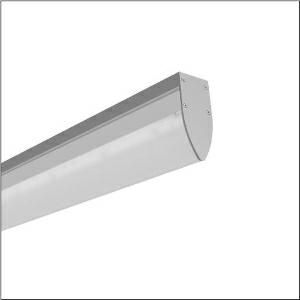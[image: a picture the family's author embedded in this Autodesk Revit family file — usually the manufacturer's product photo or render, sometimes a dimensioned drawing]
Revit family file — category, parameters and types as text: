
# Revit family: mira_21_td_51fr527d434a
name_source: partatom
category: Lighting Fixtures
units: mm (PartAtom-declared; Revit-internal decimal feet)

## family parameters
Cut with Voids When Loaded = No
Host = Face
Light Source = No
Part Type = Normal
Room Calculation Point = No
Round Connector Dimension = Use Diameter
Shared = No

## types (1)
- Mira 21 TD (1 x LED, 3660 lm, 26 W, 4000K)
    Apparent Load = 26 VA
    CIE Flux Codes = 40 68 87 81 100
    Color Rendering = 80
    Color Temperature = 4000K
    Default Elevation = 1800 mm
    Description = Mira 21 TD, clean room luminaire, primary light control with reflector, primary optical cover: cover, of PMMA, frosted, light emission: direct distribution, primary light characteristic: symmetric, installation type: surface-mounted, LED, rated luminous flux: 3.660lm, luminous efficacy: 141lm/W, light colour: 840, colour temperature: 4000K, control gear: ON/OFF, with terminal, 3-pole, max. 2.5mm², mains connection: 230V, AC, 50/60Hz, rated input power: 26W, luminaire housing, of sheet steel, coated, pure white (RAL 9010), length: 600mm, width: 55mm, height: 120mm, protection rating (complete): IP43, insulation class (complete): insulation class I (protective earthing), certification: CE, UKCA, permissible operating ambient temperature: -5..+40°C, standard: EN 50419, packaging unit: 1 piece
    Height = 120 mm
    Lamp = 1 x LED
    Lamp Light Flux = 3660 lm
    Lamp Power = 26 W
    Lamp count = 1
    Length = 600 mm
    Luminous efficacy = 141 lm/W
    Manufacturer = Siteco
    ModVariant = No
    Model = 51FR527D434A
    Mounting Place = Ceiling
    Mounting Type = Surface mounted
    Number of Poles = 1
    OnlyDefault = Yes
    Power Factor = 1
    Product Name = Mira 21 TD
    Product group = clean room luminaire | ceiling mounted
    ProductGroupID = 306
    Protection Class = Protection class I
    Protection Degree = IP 43
    RLX_Detail_Level = 1
    RLX_Emergency_Light_Flux = 0 lm
    RLX_Emergency_Type = 0
    RLX_Emergency_Type_DB = No
    RlxData = <blob elided: 25869 chars, md5=e1165511>
    Socket = socket
    Standby Power = 0 W
    System Light Flux = 3660 lm
    System Power = 26 W
    Type Comments = Product without accessories
    Type Image = l_1007115.jpg
    URL = http://relux.com
    VarID = ---
    Voltage = 0 V
    Weight = 0.00 kg
    Width = 55 mm

## geometry (parser evidence)
native form markers: Blend x4, Sweep x13
no freeform markers — native parametric forms only
